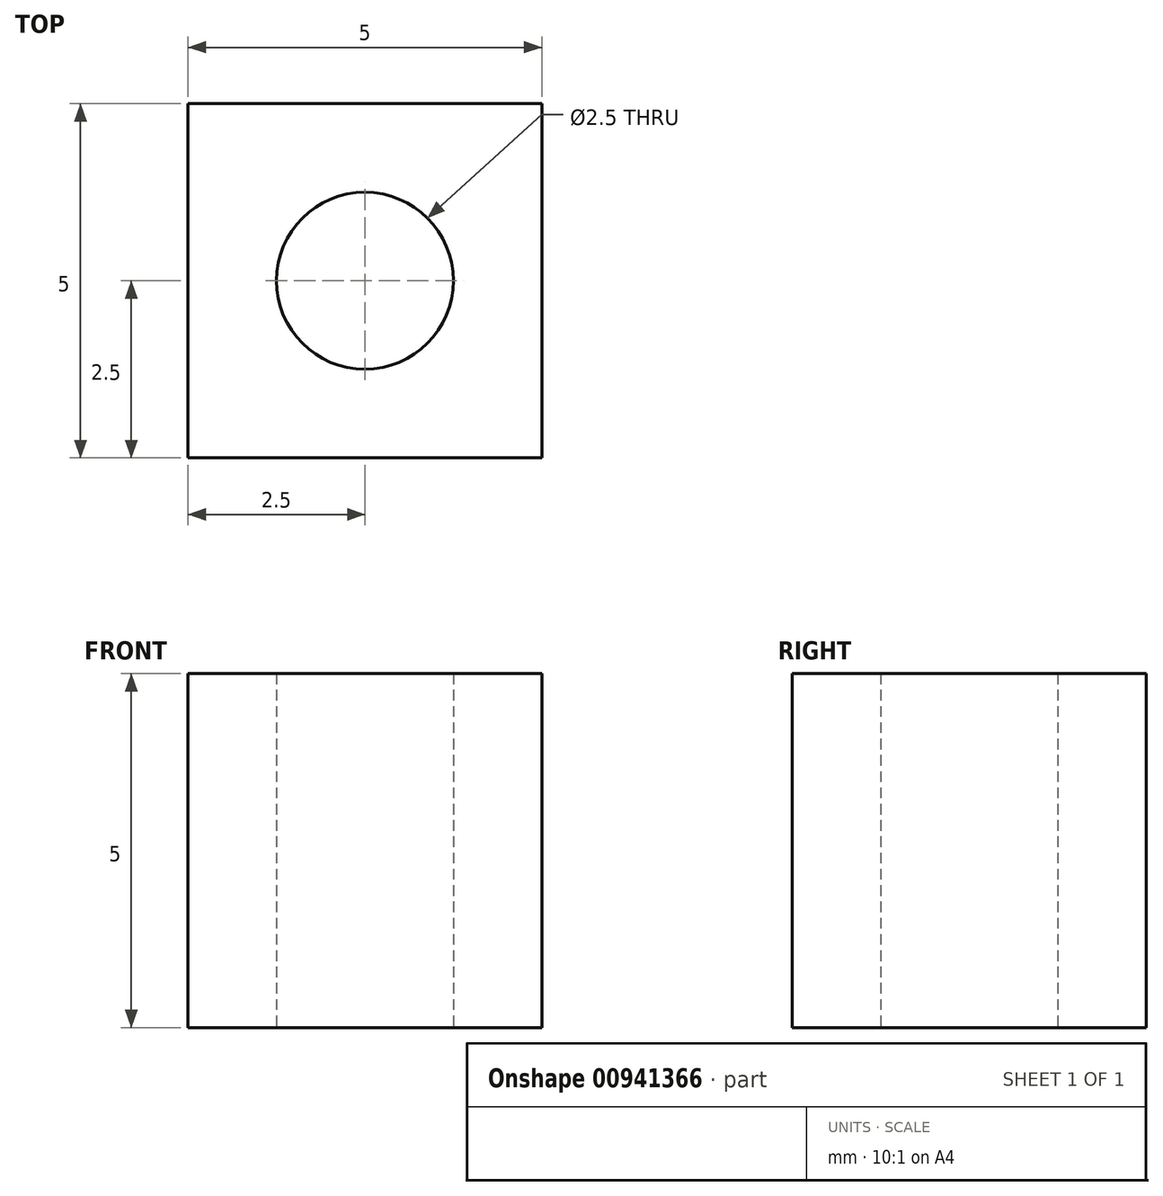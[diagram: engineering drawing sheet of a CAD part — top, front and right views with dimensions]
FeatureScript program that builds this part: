
annotation { "Feature Type Name" : "Feature", "Feature Type Description" : "" }
export const myFeature = defineFeature(function(context is Context, id is Id, definition is map)
    precondition{}
    {
        {
            var Q0;
            Q0=qCreatedBy(makeId("Top.planeOp"),FACE);
            var sketch = newSketch(context, id + "F0", { "sketchPlane" : qUnion([Q0])});
            skCircle(sketch, "E0", {"center": v(0, 0) * mm, "radius": 1.25 * mm});
            skLineSegment(sketch, "E1.bottom", {"start": v(2.5, 2.5) * mm, "end": v(-2.5, 2.5) * mm});
            skLineSegment(sketch, "E1.top", {"start": v(2.5, -2.5) * mm, "end": v(-2.5, -2.5) * mm});
            skLineSegment(sketch, "E1.left", {"start": v(2.5, 2.5) * mm, "end": v(2.5, -2.5) * mm});
            skLineSegment(sketch, "E1.right", {"start": v(-2.5, 2.5) * mm, "end": v(-2.5, -2.5) * mm});
            skSolve(sketch);
        }
        {
            var Q0;
            Q0=makeQuery(id+"F0.imprint","IMPRINT",FACE,{"disambiguationData":[TD([[makeQuery(id+"F0.imprint","IMPRINT",EDGE,{"derivedFrom":sQuery(id+"F0.wireOp",EDGE,"E0")}),-1.0]])]});
            extrude(context, id + "F1", {"entities" : qUnion([Q0]), "depth" : 5 * mm, "offsetDistance" : 25 * mm});
        }
    });
